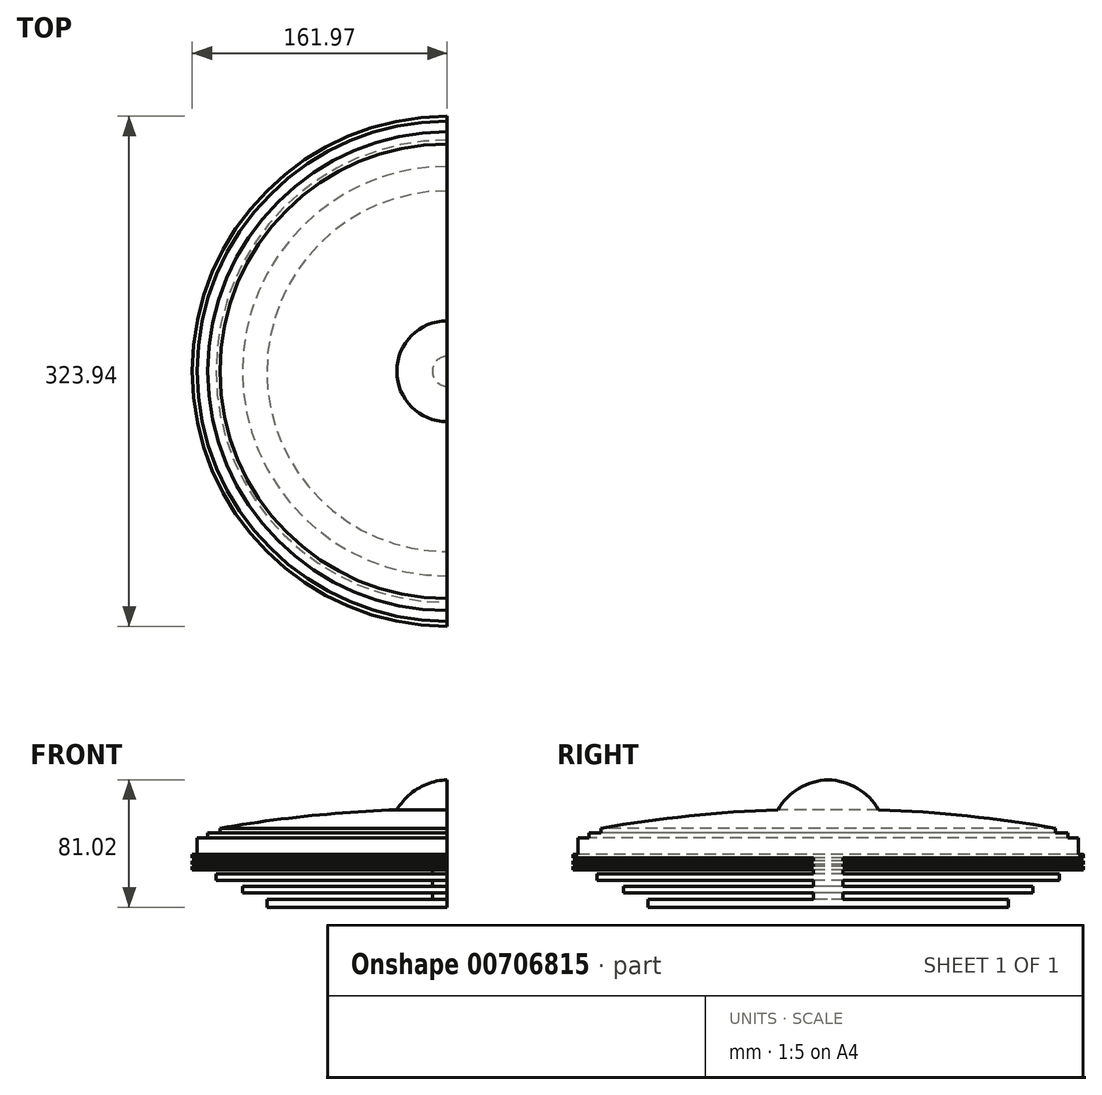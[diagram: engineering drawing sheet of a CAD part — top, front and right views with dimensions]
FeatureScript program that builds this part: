
annotation { "Feature Type Name" : "Feature", "Feature Type Description" : "" }
export const myFeature = defineFeature(function(context is Context, id is Id, definition is map)
    precondition{}
    {
        {
            var Q0;
            Q0=qCreatedBy(makeId("Front.planeOp"),FACE);
            var sketch = newSketch(context, id + "F0", { "sketchPlane" : qUnion([Q0])});
            skArc(sketch, "E0", {"start": v(-32.03, 11.7) * mm, "mid": v(-88.43, 7.75) * mm, "end": v(-144.43, 0) * mm});
            skPoint(sketch, "E1.start.orphan", {"position": v(0, 30.8) * mm});
            skArc(sketch, "E2", {"start": v(0, 30.8) * mm, "mid": v(-18.44, 25.31) * mm, "end": v(-32.03, 11.7) * mm});
            skPoint(sketch, "E3.orphan", {"position": v(0, 12.23) * mm});
            skLineSegment(sketch, "E4", {"start": v(0, 30.8) * mm, "end": v(0, 0) * mm});
            skPoint(sketch, "E5.end.orphan", {"position": v(0, -6.67) * mm});
            skLineSegment(sketch, "E6", {"start": v(-144.43, 0) * mm, "end": v(-144.43, -2.92) * mm});
            skLineSegment(sketch, "E7", {"start": v(-144.43, -2.92) * mm, "end": v(-152.07, -2.92) * mm});
            skLineSegment(sketch, "E8", {"start": v(-152.07, -2.92) * mm, "end": v(-152.07, -6.28) * mm});
            skLineSegment(sketch, "E9", {"start": v(-152.07, -6.28) * mm, "end": v(-158.88, -6.28) * mm});
            skLineSegment(sketch, "E10", {"start": v(-158.88, -6.28) * mm, "end": v(-158.88, -16.6) * mm});
            skLineSegment(sketch, "E11", {"start": v(-158.88, -16.6) * mm, "end": v(-161.97, -16.6) * mm});
            skLineSegment(sketch, "E12", {"start": v(-161.97, -16.6) * mm, "end": v(-161.97, -18.73) * mm});
            skLineSegment(sketch, "E13", {"start": v(-161.97, -18.73) * mm, "end": v(-98.16, -18.73) * mm});
            skLineSegment(sketch, "E14", {"start": v(-98.16, -20.79) * mm, "end": v(-161.97, -20.79) * mm});
            skLineSegment(sketch, "E15", {"start": v(-161.97, -20.79) * mm, "end": v(-161.97, -22.93) * mm});
            skLineSegment(sketch, "E16", {"start": v(-98.16, -24.22) * mm, "end": v(-161.97, -24.22) * mm});
            skLineSegment(sketch, "E17", {"start": v(-161.97, -24.22) * mm, "end": v(-161.97, -26.38) * mm});
            skLineSegment(sketch, "E18", {"start": v(-161.97, -26.38) * mm, "end": v(-98.16, -26.38) * mm});
            skLineSegment(sketch, "E19", {"start": v(-98.16, -29.13) * mm, "end": v(-146.85, -29.13) * mm});
            skLineSegment(sketch, "E20", {"start": v(-146.85, -29.13) * mm, "end": v(-146.85, -33.25) * mm});
            skLineSegment(sketch, "E21", {"start": v(-146.85, -33.25) * mm, "end": v(-98.16, -33.25) * mm});
            skLineSegment(sketch, "E22", {"start": v(-98.16, -36.99) * mm, "end": v(-130.08, -36.99) * mm});
            skLineSegment(sketch, "E23", {"start": v(-130.08, -36.99) * mm, "end": v(-130.08, -41.22) * mm});
            skLineSegment(sketch, "E24", {"start": v(-130.08, -41.22) * mm, "end": v(-98.16, -41.22) * mm});
            skLineSegment(sketch, "E25", {"start": v(-98.16, -45.28) * mm, "end": v(-114.55, -45.28) * mm});
            skLineSegment(sketch, "E26", {"start": v(-114.55, -45.28) * mm, "end": v(-114.55, -50.22) * mm});
            skLineSegment(sketch, "E27", {"start": v(-114.55, -50.22) * mm, "end": v(0, -50.22) * mm});
            skLineSegment(sketch, "E28", {"start": v(0, -50.22) * mm, "end": v(0, 2.44) * mm});
            skPoint(sketch, "E29.start.orphan", {"position": v(-98.16, -24.45) * mm});
            skLineSegment(sketch, "E30", {"start": v(-98.16, -18.73) * mm, "end": v(-89.4, -18.73) * mm});
            skLineSegment(sketch, "E31", {"start": v(-89.4, -18.73) * mm, "end": v(-9.44, -18.73) * mm});
            skLineSegment(sketch, "E32", {"start": v(-9.44, -18.73) * mm, "end": v(-9.44, -20.79) * mm});
            skLineSegment(sketch, "E33", {"start": v(-98.16, -20.79) * mm, "end": v(-9.44, -20.79) * mm});
            skLineSegment(sketch, "E34", {"start": v(-98.16, -24.22) * mm, "end": v(-9.44, -24.22) * mm});
            skLineSegment(sketch, "E35", {"start": v(-161.97, -22.93) * mm, "end": v(-9.44, -22.93) * mm});
            skLineSegment(sketch, "E36", {"start": v(-98.16, -26.38) * mm, "end": v(-9.44, -26.38) * mm});
            skLineSegment(sketch, "E37", {"start": v(-98.16, -29.13) * mm, "end": v(-9.44, -29.13) * mm});
            skLineSegment(sketch, "E38", {"start": v(-98.16, -33.25) * mm, "end": v(-9.44, -33.25) * mm});
            skLineSegment(sketch, "E39", {"start": v(-98.16, -36.99) * mm, "end": v(-9.44, -36.99) * mm});
            skLineSegment(sketch, "E40", {"start": v(-98.16, -41.22) * mm, "end": v(-9.44, -41.22) * mm});
            skLineSegment(sketch, "E41.trimOffspring", {"start": v(-9.44, -41.22) * mm, "end": v(-9.44, -45.28) * mm});
            skLineSegment(sketch, "E42.trimOffspring", {"start": v(-9.44, -33.25) * mm, "end": v(-9.44, -36.99) * mm});
            skLineSegment(sketch, "E43.trimOffspring", {"start": v(-9.44, -26.38) * mm, "end": v(-9.44, -29.13) * mm});
            skLineSegment(sketch, "E44.trimOffspring", {"start": v(-9.44, -22.93) * mm, "end": v(-9.44, -24.22) * mm});
            skLineSegment(sketch, "E45", {"start": v(-98.16, -45.28) * mm, "end": v(-9.44, -45.28) * mm});
            skSolve(sketch);
        }
        {
            var Q0;
            Q0=makeQuery(id+"F0.imprint","IMPRINT",FACE,{"disambiguationData":[TD([[makeQuery(id+"F0.imprint","IMPRINT",EDGE,{"derivedFrom":sQuery(id+"F0.wireOp",EDGE,"E0")}),1.0]])]});
            var Q1;
            Q1=sQuery(id+"F0.wireOp",EDGE,"E4");
            revolve(context, id + "F1", {"surfaceOperationType" : NewSurfaceOperationType.NEW, "entities" : qUnion([Q0]), "axis" : qUnion([Q1]), "revolveType" : RevolveType.SYMMETRIC, "angle" : 180 * degree});
        }
    });
